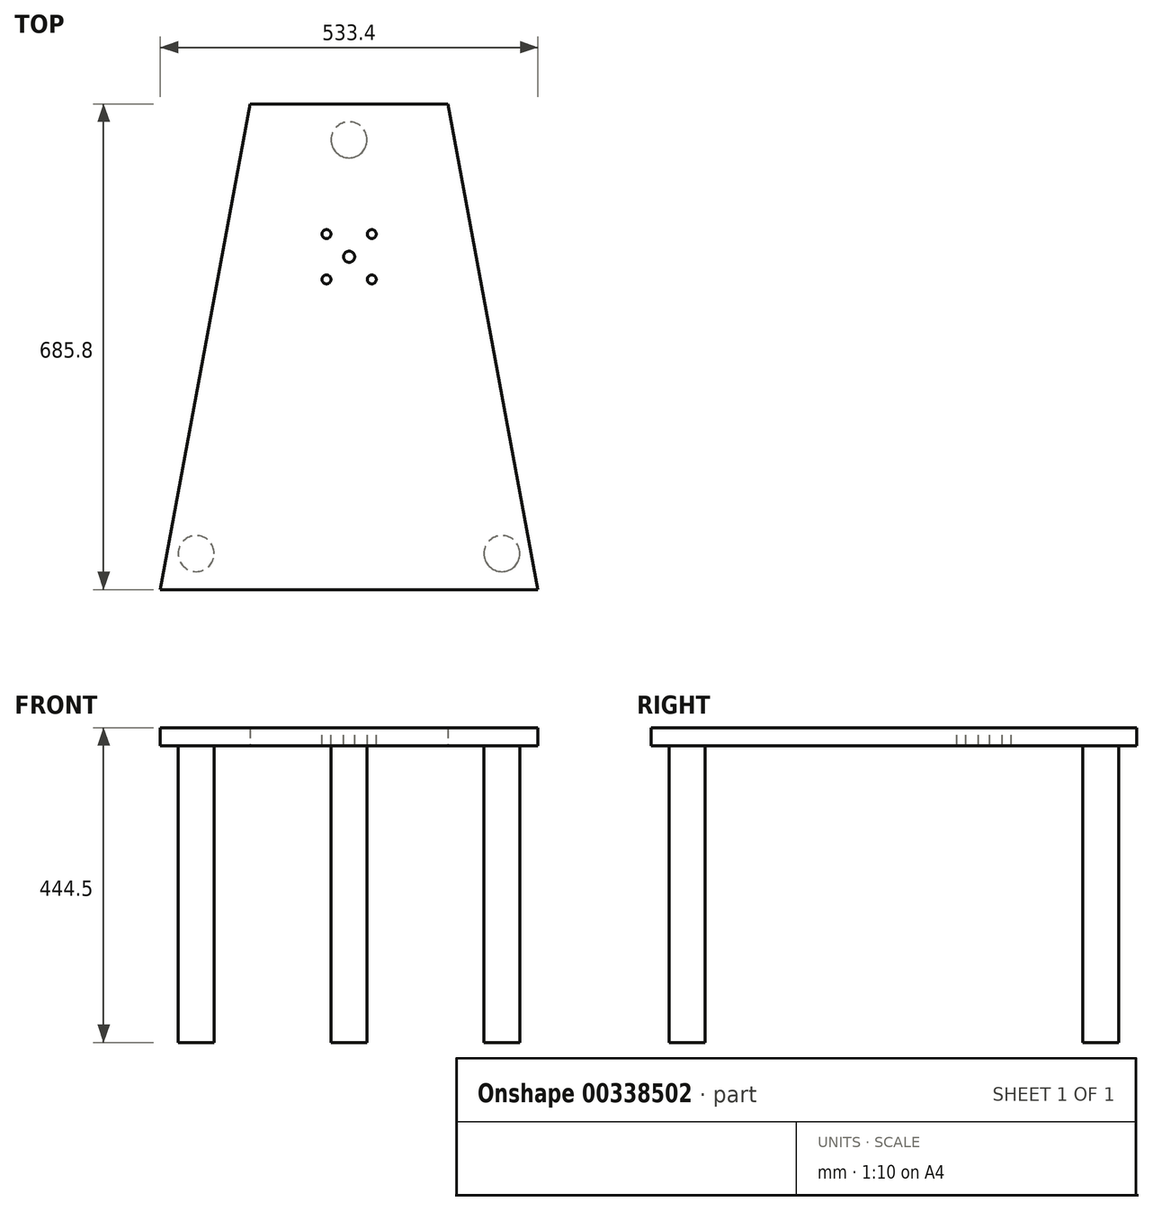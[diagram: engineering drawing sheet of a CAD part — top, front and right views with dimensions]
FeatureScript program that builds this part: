
annotation { "Feature Type Name" : "Feature", "Feature Type Description" : "" }
export const myFeature = defineFeature(function(context is Context, id is Id, definition is map)
    precondition{}
    {
        {
            var Q0;
            Q0=qCreatedBy(makeId("Top.planeOp"),FACE);
            var sketch = newSketch(context, id + "F0", { "sketchPlane" : qUnion([Q0])});
            skLineSegment(sketch, "E0", {"start": v(0, 215.9) * mm, "end": v(139.7, 215.9) * mm});
            skLineSegment(sketch, "E1", {"start": v(0, 215.9) * mm, "end": v(-139.7, 215.9) * mm});
            skLineSegment(sketch, "E2", {"start": v(0, -469.9) * mm, "end": v(-266.7, -469.9) * mm});
            skLineSegment(sketch, "E3", {"start": v(0, -469.9) * mm, "end": v(266.7, -469.9) * mm});
            skLineSegment(sketch, "E4", {"start": v(139.7, 215.9) * mm, "end": v(266.7, -469.9) * mm});
            skLineSegment(sketch, "E5", {"start": v(-139.7, 215.9) * mm, "end": v(-266.7, -469.9) * mm});
            skSolve(sketch);
        }
        {
            var Q0;
            Q0=makeQuery(id+"F0.imprint","IMPRINT",FACE,{"disambiguationData":[TD([[makeQuery(id+"F0.imprint","IMPRINT",EDGE,{"derivedFrom":sQuery(id+"F0.wireOp",EDGE,"E0")}),-1.0]])]});
            extrude(context, id + "F1", {"entities" : qUnion([Q0]), "depth" : 25.4 * mm});
        }
        {
            var Q0;
            Q0=makeQuery(id+"F1.opExtrude","CAP_FACE",FACE,{"disambiguationData":[OSD([sQuery(id+"F0.wireOp",EDGE,"E0"),sQuery(id+"F0.wireOp",EDGE,"E1"),sQuery(id+"F0.wireOp",EDGE,"E2"),sQuery(id+"F0.wireOp",EDGE,"E3"),sQuery(id+"F0.wireOp",EDGE,"E4"),sQuery(id+"F0.wireOp",EDGE,"E5")])],"isStart":true});
            var sketch = newSketch(context, id + "F2", { "sketchPlane" : qUnion([Q0])});
            skCircle(sketch, "E6", {"center": v(-215.9, 419.1) * mm, "radius": 25.4 * mm});
            skCircle(sketch, "E7", {"center": v(215.9, 419.1) * mm, "radius": 25.4 * mm});
            skCircle(sketch, "E8", {"center": v(0, -165.1) * mm, "radius": 25.4 * mm});
            skPoint(sketch, "E9", {"position": v(0, -215.9) * mm});
            skSolve(sketch);
        }
        {
            var Q0;
            Q0=makeQuery(id+"F2.imprint","IMPRINT",FACE,{"disambiguationData":[TD([[makeQuery(id+"F2.imprint","IMPRINT",EDGE,{"derivedFrom":sQuery(id+"F2.wireOp",EDGE,"E6")}),1.0]])]});
            var Q1;
            Q1=makeQuery(id+"F2.imprint","IMPRINT",FACE,{"disambiguationData":[TD([[makeQuery(id+"F2.imprint","IMPRINT",EDGE,{"derivedFrom":sQuery(id+"F2.wireOp",EDGE,"E7")}),1.0]])]});
            var Q2;
            Q2=makeQuery(id+"F2.imprint","IMPRINT",FACE,{"disambiguationData":[TD([[makeQuery(id+"F2.imprint","IMPRINT",EDGE,{"derivedFrom":sQuery(id+"F2.wireOp",EDGE,"E8")}),1.0]])]});
            extrude(context, id + "F3", {"entities" : qUnion([Q0, Q1, Q2]), "operationType" : NewBodyOperationType.ADD, "depth" : 419.1 * mm});
        }
        {
            var Q0;
            Q0=makeQuery(id+"F1.opExtrude","CAP_FACE",FACE,{"disambiguationData":[OSD([sQuery(id+"F0.wireOp",EDGE,"E0"),sQuery(id+"F0.wireOp",EDGE,"E1"),sQuery(id+"F0.wireOp",EDGE,"E2"),sQuery(id+"F0.wireOp",EDGE,"E3"),sQuery(id+"F0.wireOp",EDGE,"E4"),sQuery(id+"F0.wireOp",EDGE,"E5")])],"isStart":false});
            var sketch = newSketch(context, id + "F4", { "sketchPlane" : qUnion([Q0])});
            skPoint(sketch, "E10", {"position": v(0, 0) * mm});
            skSolve(sketch);
        }
        {
            var Q0;
            Q0=sQuery(id+"F4.wireOp",VERTEX,"E10");
            var Q1;
            Q1=makeQuery(id+"F1.opExtrude","SWEPT_BODY",BODY,{"disambiguationData":[OSD([sQuery(id+"F0.wireOp",EDGE,"E0"),sQuery(id+"F0.wireOp",EDGE,"E1"),sQuery(id+"F0.wireOp",EDGE,"E2"),sQuery(id+"F0.wireOp",EDGE,"E3"),sQuery(id+"F0.wireOp",EDGE,"E4"),sQuery(id+"F0.wireOp",EDGE,"E5")])]});
            hole(context, id + "F5", {"style" : HoleStyle.SIMPLE, "endStyle" : HoleEndStyle.THROUGH, "holeDiameter" : 15.88 * mm, "isTappedThrough" : true, "tappedDepth" : 12.7 * mm, "tapClearance" : 3, "startFromSketch" : true, "locations" : qUnion([Q0]), "scope" : qUnion([Q1])});
        }
        {
            var Q0;
            Q0=makeQuery(id+"F1.opExtrude","CAP_FACE",FACE,{"disambiguationData":[OSD([sQuery(id+"F0.wireOp",EDGE,"E0"),sQuery(id+"F0.wireOp",EDGE,"E1"),sQuery(id+"F0.wireOp",EDGE,"E2"),sQuery(id+"F0.wireOp",EDGE,"E3"),sQuery(id+"F0.wireOp",EDGE,"E4"),sQuery(id+"F0.wireOp",EDGE,"E5")])],"isStart":false});
            var sketch = newSketch(context, id + "F6", { "sketchPlane" : qUnion([Q0])});
            skLineSegment(sketch, "E11.bottom", {"start": v(32, -32) * mm, "end": v(-32, -32) * mm});
            skLineSegment(sketch, "E11.top", {"start": v(32, 32) * mm, "end": v(-32, 32) * mm});
            skLineSegment(sketch, "E11.left", {"start": v(32, -32) * mm, "end": v(32, 32) * mm});
            skLineSegment(sketch, "E11.right", {"start": v(-32, -32) * mm, "end": v(-32, 32) * mm});
            skPoint(sketch, "E12", {"position": v(0, -32) * mm});
            skPoint(sketch, "E13", {"position": v(-32, 0) * mm});
            skPoint(sketch, "E14", {"position": v(32, -32) * mm});
            skPoint(sketch, "E15", {"position": v(-32, -32) * mm});
            skPoint(sketch, "E16", {"position": v(-32, 32) * mm});
            skPoint(sketch, "E17", {"position": v(32, 32) * mm});
            skSolve(sketch);
        }
        {
            var Q0;
            Q0=sQuery(id+"F6.wireOp",VERTEX,"E14");
            var Q1;
            Q1=sQuery(id+"F6.wireOp",VERTEX,"E15");
            var Q2;
            Q2=sQuery(id+"F6.wireOp",VERTEX,"E17");
            var Q3;
            Q3=sQuery(id+"F6.wireOp",VERTEX,"E16");
            var Q4;
            Q4=makeQuery(id+"F1.opExtrude","SWEPT_BODY",BODY,{"disambiguationData":[OSD([sQuery(id+"F0.wireOp",EDGE,"E0"),sQuery(id+"F0.wireOp",EDGE,"E1"),sQuery(id+"F0.wireOp",EDGE,"E2"),sQuery(id+"F0.wireOp",EDGE,"E3"),sQuery(id+"F0.wireOp",EDGE,"E4"),sQuery(id+"F0.wireOp",EDGE,"E5")])]});
            hole(context, id + "F7", {"style" : HoleStyle.SIMPLE, "endStyle" : HoleEndStyle.THROUGH, "holeDiameter" : 12.7 * mm, "isTappedThrough" : true, "tappedDepth" : 12.7 * mm, "tapClearance" : 3, "startFromSketch" : true, "locations" : qUnion([Q0, Q1, Q2, Q3]), "scope" : qUnion([Q4])});
        }
    });
